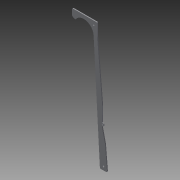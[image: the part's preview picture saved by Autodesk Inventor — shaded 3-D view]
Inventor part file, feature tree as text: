
AUTODESK INVENTOR PART (.ipt)
format: ipt  version: 2013 (Build 170138000, 138)  size: 116,224 bytes
history: native  units: in
note: dims shown in document units (in); Inventor stores cm internally (conversion verified against a paired STEP export)
features: extrude x1, fillet x1, sketch x1
ambient origin geometry x8: Origin, YZ Plane, XZ Plane, XY Plane, X Axis, Y Axis, Z Axis, Center Point
feature tree (3):
  extrude  "Extrusion4"  Depth=2.0in
  fillet  "Fillet1"  Radius=2.0in
  sketch  "Sketch1"  dims[d0=2.75in d1=30.0deg d2=2.25in d3=1.0in d4=15.5in d5=0.25in d6=0.5in d7=0.5in d8=0.1875in d9=0.3in d10=5.425in d11=0.25in d12=0.5in d13=0.5in d23=2.0in d24=2.0in d27=0.125in d28=0.0in d29=0.125in]
